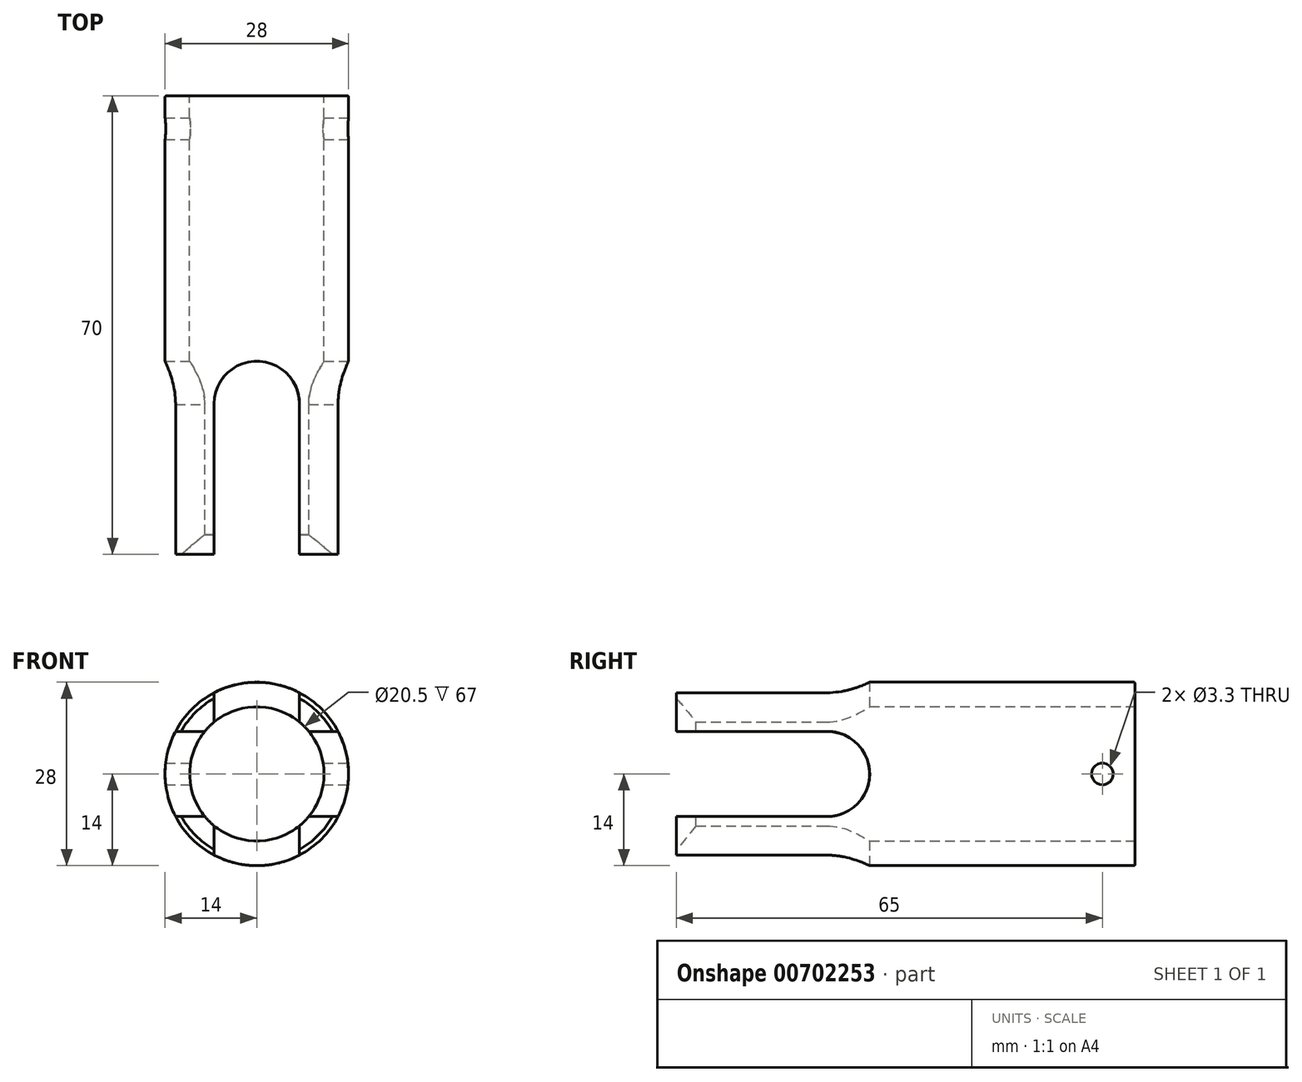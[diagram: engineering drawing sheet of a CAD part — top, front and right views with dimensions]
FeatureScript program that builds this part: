
annotation { "Feature Type Name" : "Feature", "Feature Type Description" : "" }
export const myFeature = defineFeature(function(context is Context, id is Id, definition is map)
    precondition{}
    {
        {
            var Q0;
            Q0=qCreatedBy(makeId("Front.planeOp"),FACE);
            var sketch = newSketch(context, id + "F0", { "sketchPlane" : qUnion([Q0])});
            skCircle(sketch, "E0", {"center": v(0, 0) * mm, "radius": 10.25 * mm});
            skCircle(sketch, "E1", {"center": v(0, 0) * mm, "radius": 14 * mm});
            skSolve(sketch);
        }
        {
            var Q0;
            Q0=makeQuery(id+"F0.imprint","IMPRINT",FACE,{"disambiguationData":[TD([[makeQuery(id+"F0.imprint","IMPRINT",EDGE,{"derivedFrom":sQuery(id+"F0.wireOp",EDGE,"E0")}),-1.0]])]});
            extrude(context, id + "F1", {"entities" : qUnion([Q0]), "depth" : 70 * mm, "offsetDistance" : 25 * mm});
        }
        {
            var Q0;
            Q0=qCreatedBy(makeId("Right.planeOp"),FACE);
            cPlane(context, id + "F2", {"entities" : qUnion([Q0]), "cplaneType" : CPlaneType.OFFSET, "offset" : 14 * mm, "width" : 150 * mm, "height" : 150 * mm});
        }
        {
            var Q0;
            Q0=qCreatedBy(id+"F2.planeOp",FACE);
            var sketch = newSketch(context, id + "F3", { "sketchPlane" : qUnion([Q0])});
            skPoint(sketch, "E2", {"position": v(-47, 0) * mm});
            skArc(sketch, "E3", {"start": v(-47.14, -6.5) * mm, "mid": v(-40.5, -0.07) * mm, "end": v(-47, 6.5) * mm});
            skLineSegment(sketch, "E4", {"start": v(-47.14, -6.5) * mm, "end": v(-70.06, -6.5) * mm});
            skLineSegment(sketch, "E5", {"start": v(-47, 6.5) * mm, "end": v(-70.06, 6.5) * mm});
            skLineSegment(sketch, "E6", {"start": v(-70.06, 6.5) * mm, "end": v(-70.06, -6.5) * mm});
            skPoint(sketch, "E7", {"position": v(-5, 0) * mm});
            skSolve(sketch);
        }
        {
            var Q0;
            Q0 = qSketchRegion(id + "F3", true);
            extrude(context, id + "F4", {"entities" : qUnion([Q0]), "operationType" : NewBodyOperationType.REMOVE, "oppositeDirection" : true, "depth" : 40 * mm, "offsetDistance" : 25 * mm});
        }
        {
            var Q0;
            {var subQ0=sQuery(id+"F0.wireOp",EDGE,"E0");Q0=makeQuery(id+"F4.boolean.opBoolean","SPLIT",EDGE,{"disambiguationData":[TD([makeQuery(id+"F4.opExtrude","SWEPT_FACE",FACE,{"disambiguationData":[OSD([sQuery(id+"F3.wireOp",EDGE,"E5")])]})])],"derivedFrom":makeQuery(id+"F1.opExtrude","CAP_EDGE",EDGE,{"disambiguationData":[OSD([subQ0])],"isStart":false})});}
            var Q1;
            {var subQ0=sQuery(id+"F0.wireOp",EDGE,"E0");Q1=makeQuery(id+"F4.boolean.opBoolean","SPLIT",EDGE,{"disambiguationData":[TD([makeQuery(id+"F4.opExtrude","SWEPT_FACE",FACE,{"disambiguationData":[OSD([sQuery(id+"F3.wireOp",EDGE,"E4")])]})])],"derivedFrom":makeQuery(id+"F1.opExtrude","CAP_EDGE",EDGE,{"disambiguationData":[OSD([subQ0])],"isStart":false})});}
            chamfer(context, id + "F5", {"entities" : qUnion([Q0, Q1]), "width" : 3 * mm, "tangentPropagation" : true});
        }
        {
            var Q0;
            Q0=sQuery(id+"F3.wireOp",VERTEX,"E7");
            var Q1;
            Q1=makeQuery(id+"F1.opExtrude","SWEPT_BODY",BODY,{"disambiguationData":[OSD([sQuery(id+"F0.wireOp",EDGE,"E0"),sQuery(id+"F0.wireOp",EDGE,"E1")])]});
            hole(context, id + "F6", {"style" : HoleStyle.SIMPLE, "endStyle" : HoleEndStyle.THROUGH, "standardTappedOrClearance" : lookupTablePath({ "standard" : "ISO", "engagement" : "75%", "pitch" : "0.7 mm", "size" : "M4", "type" : "Tapped" }), "standardBlindInLast" : lookupTablePath({ "standard" : "ISO", "engagement" : "75%", "pitch" : "0.7 mm", "size" : "M4", "type" : "Tapped" }), "holeDiameter" : 3.3 * mm, "majorDiameter" : 4 * mm, "showTappedDepth" : true, "isTappedThrough" : true, "tappedDepth" : 17.25 * mm, "tapClearance" : 3, "locations" : qUnion([Q0]), "scope" : qUnion([Q1])});
        }
        {
            var Q0;
            Q0=makeQuery(id+"F1.opExtrude","CAP_EDGE",EDGE,{"disambiguationData":[OSD([sQuery(id+"F0.wireOp",EDGE,"E1")])],"isStart":true});
            fillet(context, id + "F7", {"entities" : qUnion([Q0]), "radius" : .2 * mm, "tangentPropagation" : true, "allowEdgeOverflow" : false});
        }
        {
            var Q0;
            Q0=qCreatedBy(makeId("Top.planeOp"),FACE);
            cPlane(context, id + "F8", {"entities" : qUnion([Q0]), "cplaneType" : CPlaneType.OFFSET, "offset" : 14 * mm, "width" : 150 * mm, "height" : 150 * mm});
        }
        {
            var Q0;
            Q0=qCreatedBy(id+"F8.planeOp",FACE);
            var sketch = newSketch(context, id + "F9", { "sketchPlane" : qUnion([Q0])});
            skPoint(sketch, "E8", {"position": v(0, -47) * mm});
            skArc(sketch, "E9", {"start": v(6.5, -47) * mm, "mid": v(0, -40.5) * mm, "end": v(-6.5, -47) * mm});
            skLineSegment(sketch, "E10", {"start": v(6.5, -47) * mm, "end": v(6.5, -70.22) * mm});
            skLineSegment(sketch, "E11", {"start": v(-6.5, -47) * mm, "end": v(-6.5, -70.17) * mm});
            skLineSegment(sketch, "E12", {"start": v(6.5, -70.22) * mm, "end": v(-6.5, -70.17) * mm});
            skSolve(sketch);
        }
        {
            var Q0;
            Q0=makeQuery(id+"F9.imprint","IMPRINT",FACE,{"disambiguationData":[TD([[makeQuery(id+"F9.imprint","IMPRINT",EDGE,{"derivedFrom":sQuery(id+"F9.wireOp",EDGE,"E9")}),1.0]])]});
            extrude(context, id + "F10", {"entities" : qUnion([Q0]), "operationType" : NewBodyOperationType.REMOVE, "oppositeDirection" : true, "depth" : 40 * mm, "offsetDistance" : 25 * mm});
        }
    });
